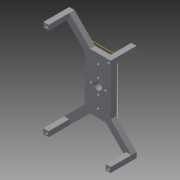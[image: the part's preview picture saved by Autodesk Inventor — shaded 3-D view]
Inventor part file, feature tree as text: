
AUTODESK INVENTOR PART (.ipt)
format: ipt  version: 2015 (Build 190159000, 159)  size: 189,952 bytes
history: native  units: in
note: dims shown in document units (in); Inventor stores cm internally (conversion verified against a paired STEP export)
features: extrude x3, sketch x3, plane x1, reference x1
ambient origin geometry x8: Origin, YZ Plane, XZ Plane, XY Plane, X Axis, Y Axis, Z Axis, Center Point
bodies: Solid1 (feature_tree)
feature tree (8):
  plane  "Work Plane1"
  extrude  "Extrusion1"  Depth=0.7874in
  extrude  "Extrusion3"  Depth=0.7874in
  extrude  "Extrusion4"  Depth=0.7874in
  sketch  "Sketch1"  dims[d0=0.1969in d1=0.0in d16=0.7874in]
  reference  "Reference1"
  sketch  "Sketch4"  dims[d17=0.7874in d18=0.7874in]
  sketch  "Sketch5"  dims[d19=0.7874in d20=0.7874in d21=0.7874in d22=0.7874in d23=0.7874in d24=0.1969in d25=0.1969in d26=0.1969in d27=0.1969in d28=0.1969in d29=0.1969in d30=0.1969in d31=0.1969in d32=0.1969in d33=0.1969in d34=0.1969in d35=0.1969in d36=0.1969in d37=0.1969in d38=0.1969in d39=0.1969in d40=0.1181in d41=0.1969in d42=0.0in d43=0.7874in d44=0.0in]
